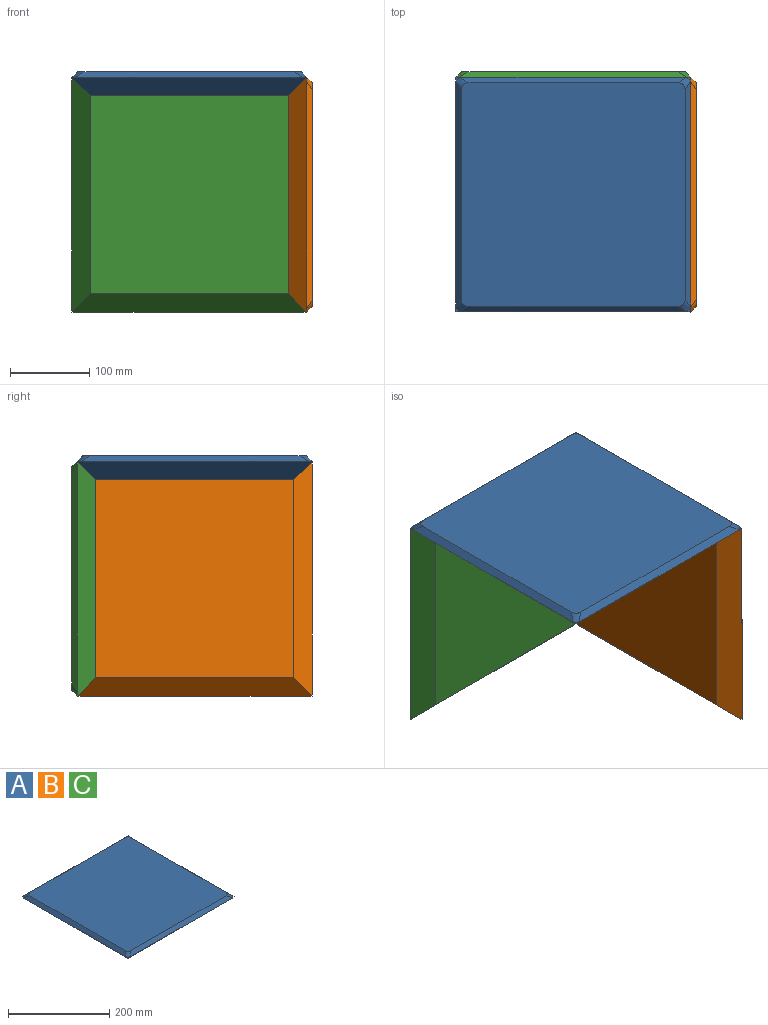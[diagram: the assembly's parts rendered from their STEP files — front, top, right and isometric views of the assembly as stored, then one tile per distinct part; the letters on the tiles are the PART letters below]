
ASSEMBLY  parts=3 mates=2
PART A: 18 faces, bbox 296x296x30 mm
  f0: plane 282x282mm, normal (0,0,1), area 79464.2mm2, adj f1,f2,f3,f4,f5,f6,f7,f8
  f1: plane 286.1x7mm, normal (0,-0.71,0.71), area 2729.6mm2, adj f0,f2,f8,f16
  f2: bspline ~15.32x15.32mm, area 118mm2, adj f0,f1,f3,f11
  f3: plane 286.1x7mm, normal (-0.71,0,0.71), area 2729.6mm2, adj f0,f2,f4,f17
  f4: bspline ~15.32x15.32mm, area 118mm2, adj f0,f3,f5,f12
  f5: plane 286.1x7mm, normal (0,0.71,0.71), area 2729.6mm2, adj f0,f4,f6,f15
  f6: bspline ~15.32x15.32mm, area 118mm2, adj f0,f5,f7,f9
  f7: plane 286.1x7mm, normal (0.71,0,0.71), area 2729.6mm2, adj f0,f6,f8,f13
  f8: bspline ~15.32x15.32mm, area 118mm2, adj f0,f1,f7,f10
  f9: plane 4.95x4.95mm, normal (0,0,1), area 12.3mm2, adj f6,f13,f15
  f10: plane 4.95x4.95mm, normal (0,0,1), area 12.3mm2, adj f8,f13,f16
  f11: plane 4.95x4.95mm, normal (0,0,1), area 12.3mm2, adj f2,f16,f17
  f12: plane 4.95x4.95mm, normal (0,0,1), area 12.3mm2, adj f4,f15,f17
  f13: plane 296x23mm, normal (0.71,0,-0.71), area 8879.8mm2, adj f7,f9,f10,f14,f15,f16
  f14: plane 250x250mm, normal (0,0,-1), area 62500mm2, adj f13,f15,f16,f17
  f15: plane 296x23mm, normal (0,0.71,-0.71), area 8879.8mm2, adj f5,f9,f12,f13,f14,f17
  f16: plane 296x23mm, normal (0,-0.71,-0.71), area 8879.8mm2, adj f1,f10,f11,f13,f14,f17
  f17: plane 296x23mm, normal (-0.71,0,-0.71), area 8879.8mm2, adj f3,f11,f12,f14,f15,f16
PART B: same geometry as A
PART C: same geometry as A
PLACE A at identity
PLACE B rot(axis=(0,1,0),90deg) t=(125,0,-125)mm
PLACE C rot(axis=(-1,0,0),90deg) t=(0,125,-125)mm
MATE fastened C.f13 <-> B.f15  axis (0.71,-0.71,0) through (136.82,136.82,-125)mm
MATE fastened B.f17 <-> A.f13  axis (-0.71,0,0.71) through (136.82,0,11.82)mm
